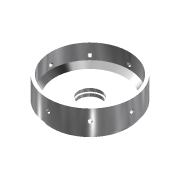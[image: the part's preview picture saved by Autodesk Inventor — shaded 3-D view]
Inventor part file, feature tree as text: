
AUTODESK INVENTOR PART (.ipt)
format: ipt  version: 2016 SP1 (Build 200210100, 210)  size: 177,152 bytes
history: native  units: in
note: dims shown in document units (in); Inventor stores cm internally (conversion verified against a paired STEP export)
features: sketch x2, revolve x1, extrude x1, pattern_circular x1
ambient origin geometry x8: Origin, YZ Plane, XZ Plane, XY Plane, X Axis, Y Axis, Z Axis, Center Point
bodies: Body1 (feature_tree)
feature tree (5):
  revolve  "Revolution3"  [1 undecoded]
  extrude  "Extrusion1"  Depth=0.1472in
  pattern_circular  "Circular Pattern1"  [2 undecoded]
  sketch  "Sketch1"  dims[d3=0.938in d8=0.625in]
  sketch  "Sketch2"  dims[d9=0.25in d10=0.1472in d11=0.1737in d12=0.2013in d26=0.2925in d28=0.0625in d29=0.3438in d30=1.875in d31=2.2851in d32=0.0625in d35=1.9526in d37=135.0deg d40=3.5156in d41=1.0in d42=1.2813in d43=90.0deg d45=0.3125in d46=8.1875in d47=0.0in d48=3.1496in d49=360.0deg d51=0.25in d53=0.936in]
note: 3 required parameter values undecoded (feature->parameter linkage not recoverable at this tier; creation-order binding heuristic only, values carry confidence <= 0.55)